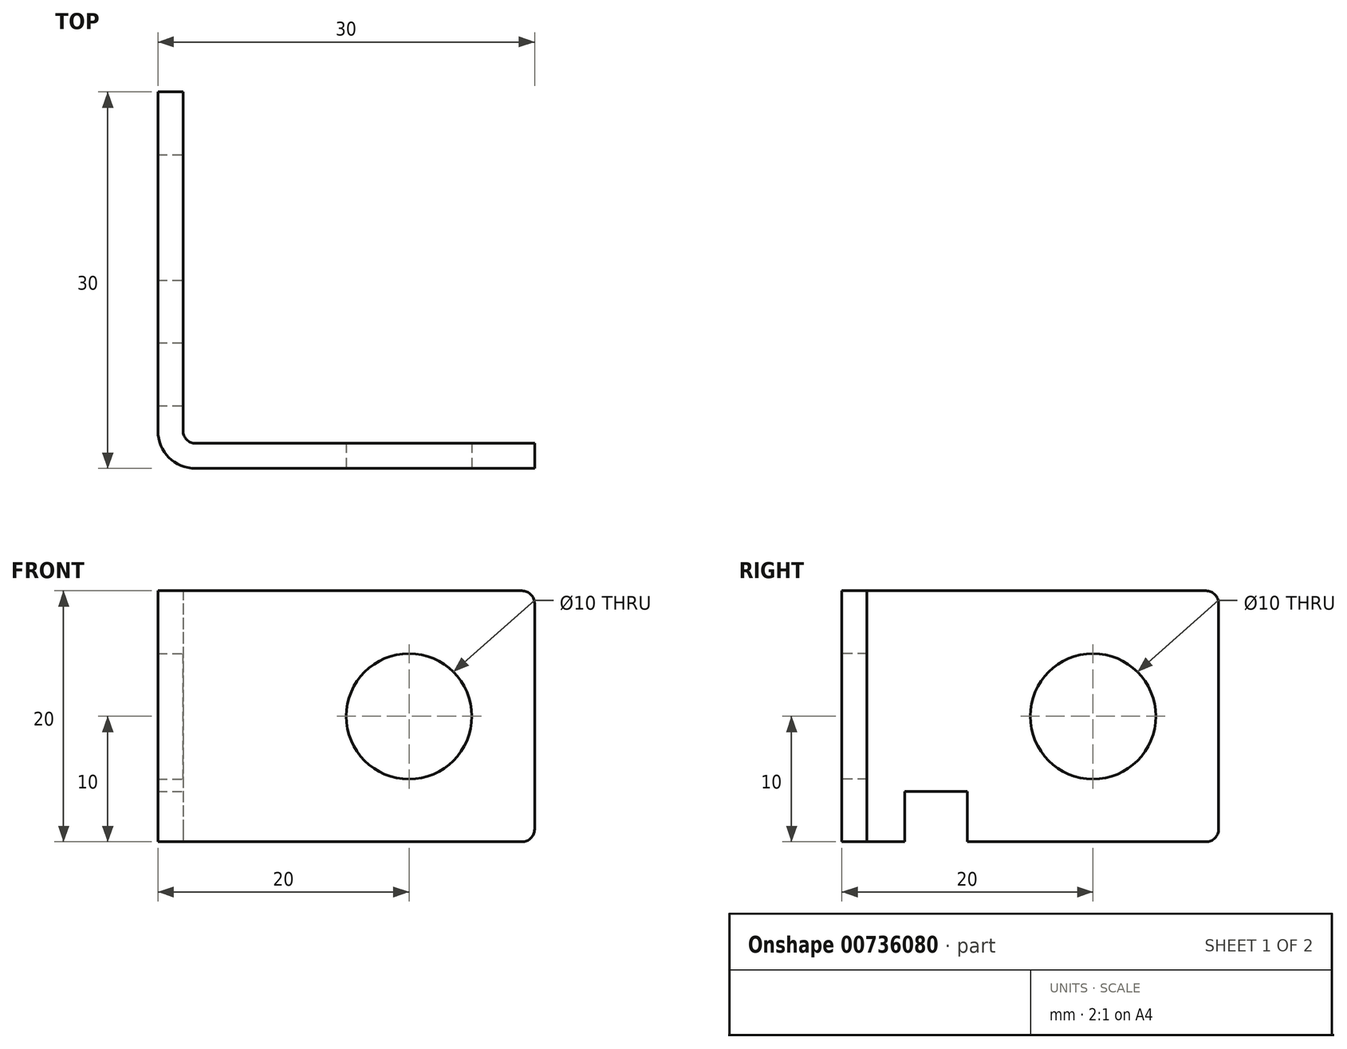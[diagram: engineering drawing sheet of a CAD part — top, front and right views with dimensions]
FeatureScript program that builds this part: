
annotation { "Feature Type Name" : "Feature", "Feature Type Description" : "" }
export const myFeature = defineFeature(function(context is Context, id is Id, definition is map)
    precondition{}
    {
        {
            var Q0;
            Q0=qCreatedBy(makeId("Top.planeOp"),FACE);
            var sketch = newSketch(context, id + "F0", { "sketchPlane" : qUnion([Q0])});
            skLineSegment(sketch, "E0", {"start": v(30, 0) * mm, "end": v(0, 0) * mm});
            skLineSegment(sketch, "E1", {"start": v(0, 0) * mm, "end": v(0, 30) * mm});
            skLineSegment(sketch, "E2.0", {"start": v(2, 2) * mm, "end": v(2, 30) * mm});
            skLineSegment(sketch, "E2.1", {"start": v(30, 2) * mm, "end": v(2, 2) * mm});
            skLineSegment(sketch, "E3", {"start": v(0, 30) * mm, "end": v(2, 30) * mm});
            skLineSegment(sketch, "E4", {"start": v(30, 2) * mm, "end": v(30, 0) * mm});
            skSolve(sketch);
        }
        {
            var Q0;
            Q0 = qSketchRegion(id + "F0", true);
            extrude(context, id + "F1", {"entities" : qUnion([Q0]), "depth" : 20 * mm, "offsetDistance" : 25 * mm});
        }
        {
            var Q0;
            Q0=makeQuery(id+"F1.opExtrude","SWEPT_FACE",FACE,{"disambiguationData":[OSD([sQuery(id+"F0.wireOp",EDGE,"E0")])]});
            var sketch = newSketch(context, id + "F2", { "sketchPlane" : qUnion([Q0])});
            skCircle(sketch, "E5", {"center": v(20, 10) * mm, "radius": 5 * mm});
            skPoint(sketch, "E5.centerSnap0", {"position": v(15, 0) * mm});
            skSolve(sketch);
        }
        {
            var Q0;
            Q0=makeQuery(id+"F1.opExtrude","SWEPT_FACE",FACE,{"disambiguationData":[OSD([sQuery(id+"F0.wireOp",EDGE,"E2.0")])]});
            var sketch = newSketch(context, id + "F3", { "sketchPlane" : qUnion([Q0])});
            skCircle(sketch, "E6", {"center": v(20, 10) * mm, "radius": 5 * mm});
            skSolve(sketch);
        }
        {
            var Q0;
            Q0 = qSketchRegion(id + "F2", true);
            extrude(context, id + "F4", {"entities" : qUnion([Q0]), "operationType" : NewBodyOperationType.REMOVE, "endBound" : BoundingType.UP_TO_NEXT, "oppositeDirection" : true, "depth" : 25 * mm, "offsetDistance" : 25 * mm});
        }
        {
            var Q0;
            Q0 = qSketchRegion(id + "F3", true);
            extrude(context, id + "F5", {"entities" : qUnion([Q0]), "operationType" : NewBodyOperationType.REMOVE, "endBound" : BoundingType.UP_TO_NEXT, "oppositeDirection" : true, "depth" : 25 * mm, "offsetDistance" : 25 * mm});
        }
        {
            var Q0;
            Q0=makeQuery(id+"F1.opExtrude","SWEPT_FACE",FACE,{"disambiguationData":[OSD([sQuery(id+"F0.wireOp",EDGE,"E2.0")])]});
            var sketch = newSketch(context, id + "F6", { "sketchPlane" : qUnion([Q0])});
            skLineSegment(sketch, "E7", {"start": v(10, 0) * mm, "end": v(10, 4) * mm});
            skLineSegment(sketch, "E8", {"start": v(10, 4) * mm, "end": v(5, 4) * mm});
            skLineSegment(sketch, "E9", {"start": v(5, 4) * mm, "end": v(5, 0) * mm});
            skSolve(sketch);
        }
        {
            var Q0;
            Q0 = qSketchRegion(id + "F6", true);
            var Q1;
            {var subQ0=sQuery(id+"F6.wireOp",EDGE,"E7");Q1=makeQuery(id+"F6.imprint","IMPRINT",FACE,{"disambiguationData":[TD([[makeQuery(id+"F6.imprint","IMPRINT",EDGE,{"derivedFrom":subQ0}),1.0]])]});}
            extrude(context, id + "F7", {"entities" : qUnion([Q0, Q1]), "operationType" : NewBodyOperationType.REMOVE, "endBound" : BoundingType.UP_TO_NEXT, "oppositeDirection" : true, "depth" : 25 * mm, "offsetDistance" : 25 * mm});
        }
        {
            var Q0;
            Q0=makeQuery(id+"F1.opExtrude","SWEPT_EDGE",EDGE,{"disambiguationData":[OSD([sQuery(id+"F0.wireOp",EDGE,"E0"),sQuery(id+"F0.wireOp",EDGE,"E1")])]});
            fillet(context, id + "F8", {"entities" : qUnion([Q0]), "radius" : 3 * mm, "tangentPropagation" : true, "allowEdgeOverflow" : false});
        }
        {
            var Q0;
            Q0=makeQuery(id+"F1.opExtrude","SWEPT_EDGE",EDGE,{"disambiguationData":[OSD([sQuery(id+"F0.wireOp",EDGE,"E2.0"),sQuery(id+"F0.wireOp",EDGE,"E2.1")])]});
            var Q1;
            Q1=makeQuery(id+"F1.opExtrude","CAP_EDGE",EDGE,{"disambiguationData":[OSD([sQuery(id+"F0.wireOp",EDGE,"E4")])],"isStart":true});
            var Q2;
            Q2=makeQuery(id+"F1.opExtrude","CAP_EDGE",EDGE,{"disambiguationData":[OSD([sQuery(id+"F0.wireOp",EDGE,"E4")])],"isStart":false});
            var Q3;
            Q3=makeQuery(id+"F1.opExtrude","CAP_EDGE",EDGE,{"disambiguationData":[OSD([sQuery(id+"F0.wireOp",EDGE,"E3")])],"isStart":true});
            var Q4;
            Q4=makeQuery(id+"F1.opExtrude","CAP_EDGE",EDGE,{"disambiguationData":[OSD([sQuery(id+"F0.wireOp",EDGE,"E3")])],"isStart":false});
            fillet(context, id + "F9", {"entities" : qUnion([Q0, Q1, Q2, Q3, Q4]), "radius" : 1 * mm, "tangentPropagation" : true, "allowEdgeOverflow" : false});
        }
    });
